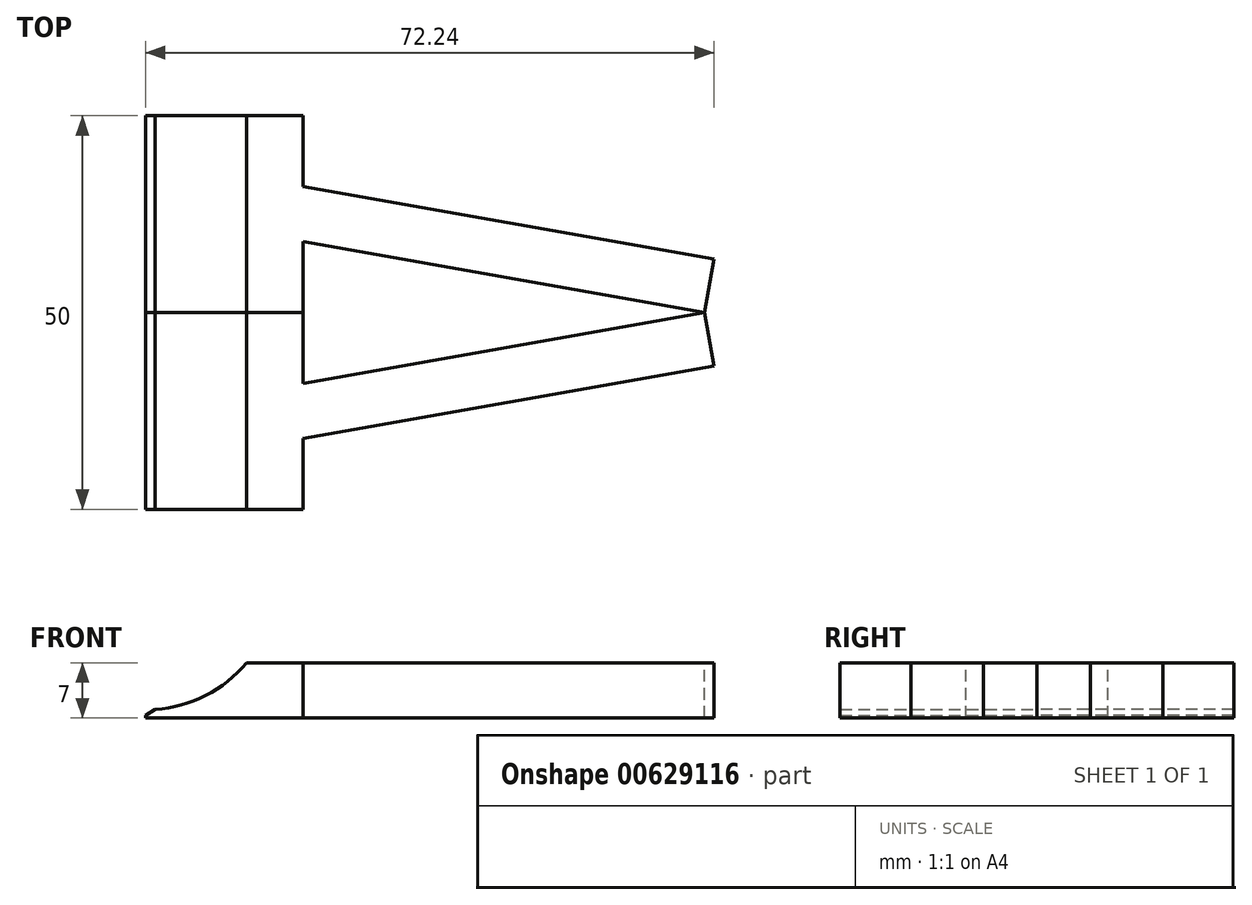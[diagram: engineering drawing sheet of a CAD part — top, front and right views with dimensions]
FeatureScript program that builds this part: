
annotation { "Feature Type Name" : "Feature", "Feature Type Description" : "" }
export const myFeature = defineFeature(function(context is Context, id is Id, definition is map)
    precondition{}
    {
        {
            var Q0;
            Q0=qCreatedBy(makeId("Front.planeOp"),FACE);
            var sketch = newSketch(context, id + "F0", { "sketchPlane" : qUnion([Q0])});
            skLineSegment(sketch, "E0", {"start": v(0, 0) * mm, "end": v(20, 0) * mm});
            skLineSegment(sketch, "E1", {"start": v(20, 0) * mm, "end": v(20, 7) * mm});
            skLineSegment(sketch, "E2", {"start": v(20, 7) * mm, "end": v(12.87, 7) * mm});
            skLineSegment(sketch, "E3", {"start": v(0, 0) * mm, "end": v(0, 1) * mm});
            skArc(sketch, "E4", {"start": v(0, 1) * mm, "mid": v(7.1, 2.57) * mm, "end": v(12.87, 7) * mm});
            skLineSegment(sketch, "E5", {"start": v(0, 1) * mm, "end": v(10, 1) * mm, "construction": true});
            skSolve(sketch);
        }
        {
            var Q0;
            Q0=makeQuery(id+"F0.imprint","IMPRINT",FACE,{"disambiguationData":[TD([[makeQuery(id+"F0.imprint","IMPRINT",EDGE,{"derivedFrom":sQuery(id+"F0.wireOp",EDGE,"E0")}),1.0]])]});
            extrude(context, id + "F1", {"entities" : qUnion([Q0]), "depth" : 25 * mm, "offsetDistance" : 25 * mm});
        }
        {
            var Q0;
            Q0=makeQuery(id+"F1.opExtrude","SWEPT_EDGE",EDGE,{"disambiguationData":[OSD([sQuery(id+"F0.wireOp",EDGE,"E3"),sQuery(id+"F0.wireOp",EDGE,"E4")])]});
            chamfer(context, id + "F2", {"entities" : qUnion([Q0]), "chamferType" : ChamferType.OFFSET_ANGLE, "width" : .75 * mm, "oppositeDirection" : false, "angle" : 60 * degree, "tangentPropagation" : true});
        }
        {
            var Q0;
            Q0=makeQuery(id+"F1.opExtrude","SWEPT_FACE",FACE,{"disambiguationData":[OSD([sQuery(id+"F0.wireOp",EDGE,"E2")])]});
            var sketch = newSketch(context, id + "F3", { "sketchPlane" : qUnion([Q0])});
            skLineSegment(sketch, "E6", {"start": v(20, -9) * mm, "end": v(71.04, 0) * mm});
            skLineSegment(sketch, "E7", {"start": v(20, -16) * mm, "end": v(72.24, -6.79) * mm});
            skLineSegment(sketch, "E8", {"start": v(71.04, 0) * mm, "end": v(72.24, -6.79) * mm});
            skSolve(sketch);
        }
        {
            var Q0;
            {var subQ0=sQuery(id+"F3.wireOp",EDGE,"E6");Q0=makeQuery(id+"F3.imprint","IMPRINT",FACE,{"disambiguationData":[TD([[makeQuery(id+"F3.imprint","IMPRINT",EDGE,{"derivedFrom":subQ0}),-1.0]])]});}
            var Q1;
            Q1=makeQuery(id+"F1.opExtrude","SWEPT_FACE",FACE,{"disambiguationData":[OSD([sQuery(id+"F0.wireOp",EDGE,"E0")])]});
            extrude(context, id + "F4", {"entities" : qUnion([Q0]), "operationType" : NewBodyOperationType.ADD, "endBound" : BoundingType.UP_TO_SURFACE, "oppositeDirection" : true, "depth" : 25 * mm, "endBoundEntityFace" : qUnion([Q1]), "offsetDistance" : 25 * mm});
        }
        {
            var Q0;
            Q0=makeQuery(id+"F1.opExtrude","SWEPT_BODY",BODY,{"disambiguationData":[OSD([sQuery(id+"F0.wireOp",EDGE,"E0"),sQuery(id+"F0.wireOp",EDGE,"E1"),sQuery(id+"F0.wireOp",EDGE,"E2"),sQuery(id+"F0.wireOp",EDGE,"E3"),sQuery(id+"F0.wireOp",EDGE,"E4")])]});
            var Q1;
            Q1=qCreatedBy(makeId("Front.planeOp"),FACE);
            mirror(context, id + "F5", {"entities" : qUnion([Q0]), "mirrorPlane" : qUnion([Q1])});
        }
    });
